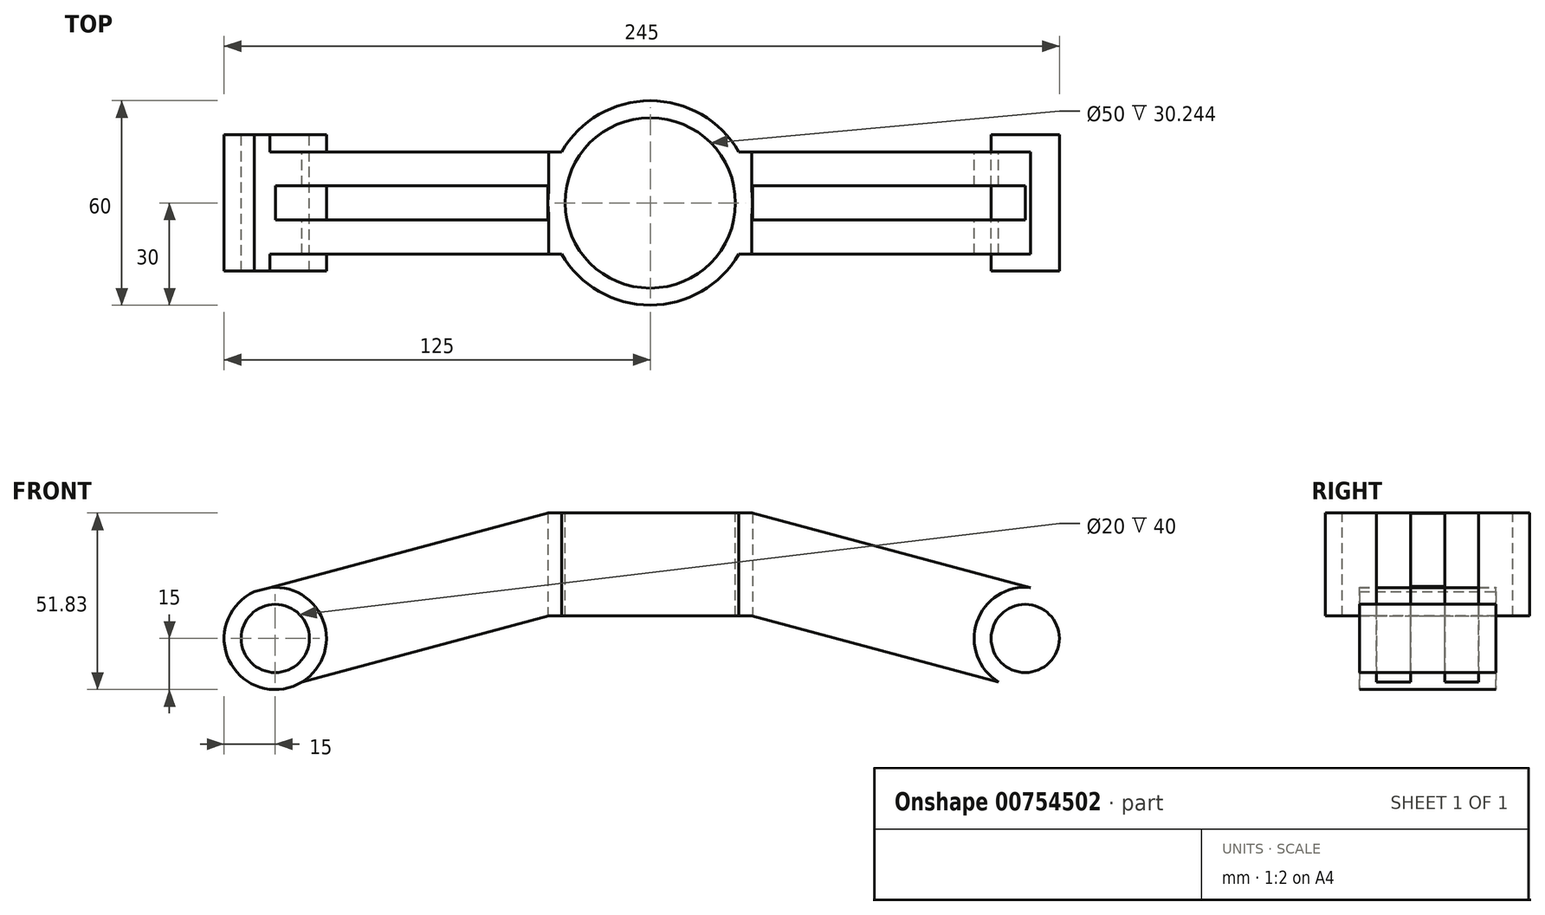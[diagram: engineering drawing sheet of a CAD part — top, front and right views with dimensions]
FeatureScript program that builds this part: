
annotation { "Feature Type Name" : "Feature", "Feature Type Description" : "" }
export const myFeature = defineFeature(function(context is Context, id is Id, definition is map)
    precondition{}
    {
        {
            var Q0;
            Q0=qCreatedBy(makeId("Front.planeOp"),FACE);
            var sketch = newSketch(context, id + "F0", { "sketchPlane" : qUnion([Q0])});
            skCircle(sketch, "E0", {"center": v(-110, 0) * mm, "radius": 10 * mm});
            skCircle(sketch, "E1", {"center": v(-110, 0) * mm, "radius": 15 * mm});
            skLineSegment(sketch, "E2", {"start": v(-110, 0) * mm, "end": v(110, 0) * mm, "construction": true});
            skLineSegment(sketch, "E3", {"start": v(-102.2, -12.82) * mm, "end": v(-29.8, 6.58) * mm});
            skLineSegment(sketch, "E4", {"start": v(-29.8, 6.58) * mm, "end": v(0, 6.58) * mm});
            skLineSegment(sketch, "E5", {"start": v(-116.1, 13.7) * mm, "end": v(-29.8, 36.83) * mm});
            skLineSegment(sketch, "E6", {"start": v(-29.8, 36.83) * mm, "end": v(0, 36.83) * mm});
            skCircle(sketch, "E7.MirrorC", {"center": v(110, 0) * mm, "radius": 10 * mm});
            skCircle(sketch, "E8.MirrorC", {"center": v(110, 0) * mm, "radius": 15 * mm});
            skLineSegment(sketch, "E9.MirrorCS", {"start": v(29.8, 6.58) * mm, "end": v(0, 6.58) * mm});
            skLineSegment(sketch, "E10.MirrorCS", {"start": v(102.2, -12.82) * mm, "end": v(29.8, 6.58) * mm});
            skLineSegment(sketch, "E11.MirrorCS", {"start": v(29.8, 36.83) * mm, "end": v(0, 36.83) * mm});
            skLineSegment(sketch, "E12.MirrorCS", {"start": v(116.1, 13.7) * mm, "end": v(29.8, 36.83) * mm});
            skLineSegment(sketch, "E13", {"start": v(-29.8, 36.83) * mm, "end": v(-29.8, 6.58) * mm});
            skLineSegment(sketch, "E14", {"start": v(29.8, 36.83) * mm, "end": v(29.8, 6.58) * mm});
            skSolve(sketch);
        }
        {
            var Q0;
            {var subQ0=sQuery(id+"F0.wireOp",EDGE,"E3");Q0=makeQuery(id+"F0.imprint","IMPRINT",FACE,{"disambiguationData":[TD([[makeQuery(id+"F0.imprint","IMPRINT",EDGE,{"derivedFrom":subQ0}),1.0]])]});}
            var Q1;
            Q1=makeQuery(id+"F0.imprint","IMPRINT",FACE,{"disambiguationData":[TD([[makeQuery(id+"F0.imprint","IMPRINT",EDGE,{"derivedFrom":sQuery(id+"F0.wireOp",EDGE,"E4")}),1.0]])]});
            var Q2;
            {var subQ0=sQuery(id+"F0.wireOp",EDGE,"E10.MirrorCS");Q2=makeQuery(id+"F0.imprint","IMPRINT",FACE,{"disambiguationData":[TD([[makeQuery(id+"F0.imprint","IMPRINT",EDGE,{"derivedFrom":subQ0}),-1.0]])]});}
            extrude(context, id + "F1", {"entities" : qUnion([Q0, Q1, Q2]), "endBound" : BoundingType.SYMMETRIC, "depth" : 30 * mm, "offsetDistance" : 25.4 * mm});
        }
        {
            var Q0;
            Q0=makeQuery(id+"F0.imprint","IMPRINT",FACE,{"disambiguationData":[TD([[makeQuery(id+"F0.imprint","IMPRINT",EDGE,{"derivedFrom":sQuery(id+"F0.wireOp",EDGE,"E0")}),-1.0]])]});
            var Q1;
            Q1=makeQuery(id+"F0.imprint","IMPRINT",FACE,{"disambiguationData":[TD([[makeQuery(id+"F0.imprint","IMPRINT",EDGE,{"derivedFrom":sQuery(id+"F0.wireOp",EDGE,"E7.MirrorC")}),1.0]])]});
            extrude(context, id + "F2", {"entities" : qUnion([Q0, Q1]), "operationType" : NewBodyOperationType.ADD, "endBound" : BoundingType.SYMMETRIC, "depth" : 40 * mm, "offsetDistance" : 25.4 * mm});
        }
        {
            var Q0;
            Q0=makeQuery(id+"F1.opExtrude","SWEPT_FACE",FACE,{"disambiguationData":[OSD([sQuery(id+"F0.wireOp",EDGE,"E6"),sQuery(id+"F0.wireOp",EDGE,"E11.MirrorCS")])]});
            var sketch = newSketch(context, id + "F3", { "sketchPlane" : qUnion([Q0])});
            skCircle(sketch, "E15", {"center": v(0, 0) * mm, "radius": 30 * mm});
            skCircle(sketch, "E16", {"center": v(0, 0) * mm, "radius": 25 * mm});
            skSolve(sketch);
        }
        {
            var Q0;
            Q0 = qSketchRegion(id + "F3", true);
            var Q1;
            Q1=makeQuery(id+"F1.opExtrude","SWEPT_FACE",FACE,{"disambiguationData":[OSD([sQuery(id+"F0.wireOp",EDGE,"E4"),sQuery(id+"F0.wireOp",EDGE,"E9.MirrorCS")])]});
            extrude(context, id + "F4", {"entities" : qUnion([Q0]), "operationType" : NewBodyOperationType.ADD, "endBound" : BoundingType.UP_TO_SURFACE, "oppositeDirection" : true, "depth" : 25.4 * mm, "endBoundEntityFace" : qUnion([Q1]), "offsetDistance" : 25.4 * mm});
        }
        {
            var Q0;
            {var subQ0=sQuery(id+"F3.wireOp",EDGE,"E16");var subQ1=sQuery(id+"F0.wireOp",EDGE,"E11.MirrorCS");var subQ2=sQuery(id+"F0.wireOp",EDGE,"E6");var subQ3=makeQuery(id+"F1.opExtrude","CAP_EDGE",EDGE,{"disambiguationData":[OSD([subQ2,subQ1])],"isStart":true});var subQ4=makeQuery(id+"F3.imprint","INTERSECT",VERTEX,{"disambiguationData":[OD(0.0)],"derivedFrom":[subQ3,subQ0]});Q0=makeQuery(id+"F3.imprint","IMPRINT",FACE,{"disambiguationData":[TD([[makeQuery(id+"F3.imprint","IMPRINT",EDGE,{"disambiguationData":[TD([[subQ4,-1.0]])],"derivedFrom":subQ0}),1.0]])]});}
            extrude(context, id + "F5", {"entities" : qUnion([Q0]), "operationType" : NewBodyOperationType.REMOVE, "endBound" : BoundingType.THROUGH_ALL, "oppositeDirection" : true, "depth" : 25.4 * mm, "offsetDistance" : 25.4 * mm});
        }
        {
            var Q0;
            Q0=qCreatedBy(makeId("Top.planeOp"),FACE);
            cPlane(context, id + "F6", {"entities" : qUnion([Q0]), "cplaneType" : CPlaneType.OFFSET, "offset" : 25 * mm, "oppositeDirection" : true, "width" : 150 * mm, "height" : 150 * mm});
        }
        {
            var Q0;
            Q0=qCreatedBy(id+"F6.planeOp",FACE);
            var sketch = newSketch(context, id + "F7", { "sketchPlane" : qUnion([Q0])});
            skLineSegment(sketch, "E17", {"start": v(-109.93, -5) * mm, "end": v(110.07, -5) * mm});
            skLineSegment(sketch, "E18.MirrorCS", {"start": v(-109.93, 5) * mm, "end": v(110.07, 5) * mm});
            skLineSegment(sketch, "E19", {"start": v(-109.93, -5) * mm, "end": v(-109.93, 5) * mm});
            skLineSegment(sketch, "E20", {"start": v(110.07, -5) * mm, "end": v(110.07, 5) * mm});
            skLineSegment(sketch, "E21", {"start": v(-30, -5) * mm, "end": v(-30, 5) * mm});
            skLineSegment(sketch, "E22", {"start": v(30, -5) * mm, "end": v(30, 5) * mm});
            skSolve(sketch);
        }
        {
            var Q0;
            {var subQ0=sQuery(id+"F7.wireOp",EDGE,"E19");Q0=makeQuery(id+"F7.imprint","IMPRINT",FACE,{"disambiguationData":[TD([[makeQuery(id+"F7.imprint","IMPRINT",EDGE,{"derivedFrom":subQ0}),-1.0]])]});}
            var Q1;
            {var subQ0=sQuery(id+"F7.wireOp",EDGE,"E20");Q1=makeQuery(id+"F7.imprint","IMPRINT",FACE,{"disambiguationData":[TD([[makeQuery(id+"F7.imprint","IMPRINT",EDGE,{"derivedFrom":subQ0}),1.0]])]});}
            extrude(context, id + "F8", {"entities" : qUnion([Q0, Q1]), "operationType" : NewBodyOperationType.REMOVE, "endBound" : BoundingType.THROUGH_ALL, "depth" : 25 * mm, "offsetDistance" : 25 * mm});
        }
        {
            var Q0;
            Q0=makeQuery(id+"F0.imprint","IMPRINT",FACE,{"disambiguationData":[TD([[makeQuery(id+"F0.imprint","IMPRINT",EDGE,{"derivedFrom":sQuery(id+"F0.wireOp",EDGE,"E0")}),-1.0]])]});
            var Q1;
            Q1=makeQuery(id+"F0.imprint","IMPRINT",FACE,{"disambiguationData":[TD([[makeQuery(id+"F0.imprint","IMPRINT",EDGE,{"derivedFrom":sQuery(id+"F0.wireOp",EDGE,"E7.MirrorC")}),1.0]])]});
            extrude(context, id + "F9", {"entities" : qUnion([Q0, Q1]), "operationType" : NewBodyOperationType.ADD, "endBound" : BoundingType.SYMMETRIC, "depth" : 10 * mm, "offsetDistance" : 25 * mm});
        }
    });
